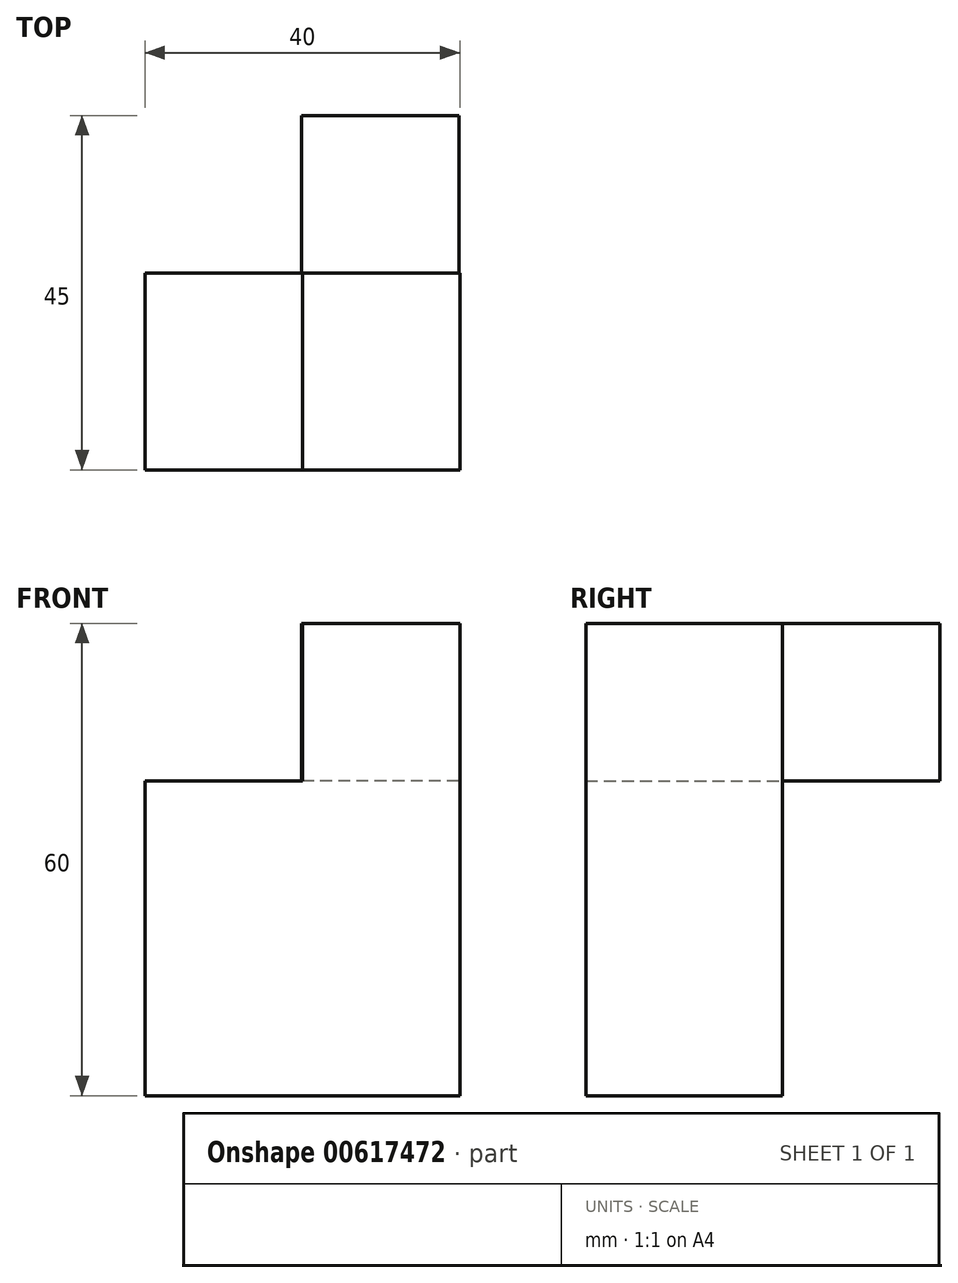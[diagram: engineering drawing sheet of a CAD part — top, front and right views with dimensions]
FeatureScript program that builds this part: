
annotation { "Feature Type Name" : "Feature", "Feature Type Description" : "" }
export const myFeature = defineFeature(function(context is Context, id is Id, definition is map)
    precondition{}
    {
        {
            var Q0;
            Q0=qCreatedBy(makeId("Front.planeOp"),FACE);
            var sketch = newSketch(context, id + "F0", { "sketchPlane" : qUnion([Q0])});
            skLineSegment(sketch, "E0", {"start": v(-33.63, 15.93) * mm, "end": v(-33.63, -24.07) * mm});
            skLineSegment(sketch, "E1", {"start": v(-33.63, -24.07) * mm, "end": v(6.37, -24.07) * mm});
            skLineSegment(sketch, "E2", {"start": v(6.37, -24.07) * mm, "end": v(6.37, 35.93) * mm});
            skLineSegment(sketch, "E3", {"start": v(6.37, 35.93) * mm, "end": v(-13.63, 35.93) * mm});
            skLineSegment(sketch, "E4", {"start": v(-13.63, 35.93) * mm, "end": v(-13.63, 15.93) * mm});
            skLineSegment(sketch, "E5", {"start": v(-13.63, 15.93) * mm, "end": v(-33.63, 15.93) * mm});
            skSolve(sketch);
        }
        {
            var Q0;
            Q0=makeQuery(id+"F0.imprint","IMPRINT",FACE,{"disambiguationData":[TD([[makeQuery(id+"F0.imprint","IMPRINT",EDGE,{"derivedFrom":sQuery(id+"F0.wireOp",EDGE,"E0")}),1.0]])]});
            extrude(context, id + "F1", {"entities" : qUnion([Q0]), "depth" : 25 * mm, "offsetDistance" : 25 * mm});
        }
        {
            var Q0;
            Q0=qCreatedBy(makeId("Front.planeOp"),FACE);
            var sketch = newSketch(context, id + "F2", { "sketchPlane" : qUnion([Q0])});
            skLineSegment(sketch, "E6", {"start": v(-13.77, 35.9) * mm, "end": v(6.23, 35.9) * mm});
            skLineSegment(sketch, "E7", {"start": v(6.23, 35.9) * mm, "end": v(6.23, 15.9) * mm});
            skLineSegment(sketch, "E8", {"start": v(6.23, 15.9) * mm, "end": v(-13.77, 15.9) * mm});
            skLineSegment(sketch, "E9", {"start": v(-13.77, 15.9) * mm, "end": v(-13.77, 35.9) * mm});
            skSolve(sketch);
        }
        {
            var Q0;
            Q0 = qSketchRegion(id + "F2", true);
            extrude(context, id + "F3", {"entities" : qUnion([Q0]), "operationType" : NewBodyOperationType.ADD, "depth" : -20 * mm, "offsetDistance" : 25 * mm});
        }
    });
